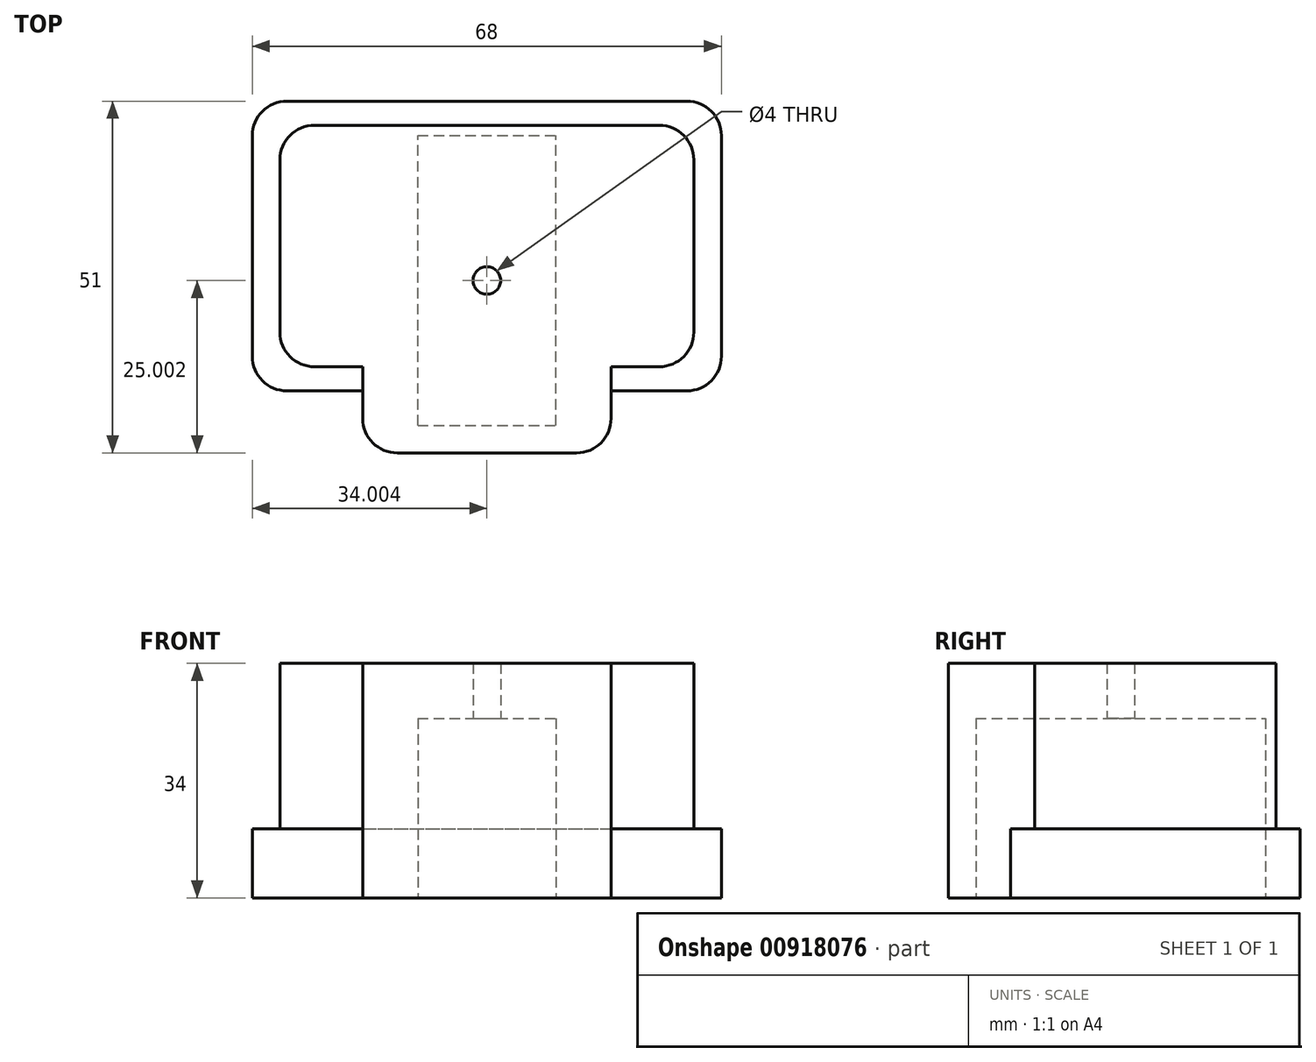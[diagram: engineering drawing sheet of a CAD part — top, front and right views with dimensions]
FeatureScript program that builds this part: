
annotation { "Feature Type Name" : "Feature", "Feature Type Description" : "" }
export const myFeature = defineFeature(function(context is Context, id is Id, definition is map)
    precondition{}
    {
        {
            var Q0;
            Q0=qCreatedBy(makeId("Top.planeOp"),FACE);
            var sketch = newSketch(context, id + "F0", { "sketchPlane" : qUnion([Q0])});
            skLineSegment(sketch, "E0.bottom", {"start": v(-57.16, -32.25) * mm, "end": v(10.84, -32.25) * mm});
            skLineSegment(sketch, "E0.top", {"start": v(-57.16, -74.25) * mm, "end": v(10.84, -74.25) * mm});
            skLineSegment(sketch, "E0.left", {"start": v(-57.16, -32.25) * mm, "end": v(-57.16, -74.25) * mm});
            skLineSegment(sketch, "E0.right", {"start": v(10.84, -32.25) * mm, "end": v(10.84, -74.25) * mm});
            skSolve(sketch);
        }
        {
            var Q0;
            Q0 = qSketchRegion(id + "F0", true);
            extrude(context, id + "F1", {"entities" : qUnion([Q0]), "flatOperationType" : FlatOperationType.REMOVE, "depth" : 10 * mm, "offsetDistance" : 25 * mm, "domain" : OperationDomain.MODEL});
        }
        {
            var Q0;
            Q0=makeQuery(id+"F1.opExtrude","CAP_FACE",FACE,{"disambiguationData":[OSD([sQuery(id+"F0.wireOp",EDGE,"E0.bottom"),sQuery(id+"F0.wireOp",EDGE,"E0.top"),sQuery(id+"F0.wireOp",EDGE,"E0.left"),sQuery(id+"F0.wireOp",EDGE,"E0.right")])],"isStart":false});
            var sketch = newSketch(context, id + "F2", { "sketchPlane" : qUnion([Q0])});
            skLineSegment(sketch, "E1", {"start": v(-57.16, -32.25) * mm, "end": v(10.84, -74.25) * mm});
            skPoint(sketch, "E2", {"position": v(-23.16, -53.25) * mm});
            skLineSegment(sketch, "E3.bottom", {"start": v(-53.16, -35.75) * mm, "end": v(6.84, -35.75) * mm});
            skLineSegment(sketch, "E3.top", {"start": v(-53.16, -70.75) * mm, "end": v(6.84, -70.75) * mm});
            skLineSegment(sketch, "E3.left", {"start": v(-53.16, -35.75) * mm, "end": v(-53.16, -70.75) * mm});
            skLineSegment(sketch, "E3.right", {"start": v(6.84, -35.75) * mm, "end": v(6.84, -70.75) * mm});
            skLineSegment(sketch, "E4", {"start": v(6.84, -35.75) * mm, "end": v(-53.16, -70.75) * mm});
            skSolve(sketch);
        }
        {
            var Q0;
            Q0 = qSketchRegion(id + "F2", true);
            extrude(context, id + "F3", {"entities" : qUnion([Q0]), "operationType" : NewBodyOperationType.ADD, "depth" : 24 * mm, "offsetDistance" : 25 * mm});
        }
        {
            var Q0;
            Q0=makeQuery(id+"F1.opExtrude","CAP_FACE",FACE,{"disambiguationData":[OSD([sQuery(id+"F0.wireOp",EDGE,"E0.bottom"),sQuery(id+"F0.wireOp",EDGE,"E0.top"),sQuery(id+"F0.wireOp",EDGE,"E0.left"),sQuery(id+"F0.wireOp",EDGE,"E0.right")])],"isStart":true});
            var sketch = newSketch(context, id + "F4", { "sketchPlane" : qUnion([Q0])});
            skLineSegment(sketch, "E5.bottom", {"start": v(-5.16, 37.25) * mm, "end": v(-41.16, 37.25) * mm});
            skLineSegment(sketch, "E5.top", {"start": v(-5.16, 83.25) * mm, "end": v(-41.16, 83.25) * mm});
            skLineSegment(sketch, "E5.left", {"start": v(-5.16, 37.25) * mm, "end": v(-5.16, 83.25) * mm});
            skLineSegment(sketch, "E5.right", {"start": v(-41.16, 37.25) * mm, "end": v(-41.16, 83.25) * mm});
            skPoint(sketch, "E6", {"position": v(-23.16, 32.25) * mm});
            skPoint(sketch, "E7", {"position": v(-23.16, 37.25) * mm});
            skSolve(sketch);
        }
        {
            var Q0;
            Q0 = qSketchRegion(id + "F4", true);
            extrude(context, id + "F5", {"entities" : qUnion([Q0]), "operationType" : NewBodyOperationType.ADD, "flatOperationType" : FlatOperationType.REMOVE, "oppositeDirection" : true, "depth" : 34 * mm, "offsetDistance" : 25 * mm, "domain" : OperationDomain.MODEL});
        }
        {
            var Q0;
            Q0=makeQuery(id+"F1.opExtrude","CAP_FACE",FACE,{"disambiguationData":[OSD([sQuery(id+"F0.wireOp",EDGE,"E0.bottom"),sQuery(id+"F0.wireOp",EDGE,"E0.top"),sQuery(id+"F0.wireOp",EDGE,"E0.left"),sQuery(id+"F0.wireOp",EDGE,"E0.right")])],"isStart":true});
            var sketch = newSketch(context, id + "F6", { "sketchPlane" : qUnion([Q0])});
            skLineSegment(sketch, "E8.bottom", {"start": v(-33.16, 79.25) * mm, "end": v(-13.16, 79.25) * mm});
            skLineSegment(sketch, "E8.top", {"start": v(-33.16, 37.25) * mm, "end": v(-13.16, 37.25) * mm});
            skLineSegment(sketch, "E8.left", {"start": v(-33.16, 79.25) * mm, "end": v(-33.16, 37.25) * mm});
            skLineSegment(sketch, "E8.right", {"start": v(-13.16, 79.25) * mm, "end": v(-13.16, 37.25) * mm});
            skSolve(sketch);
        }
        {
            var Q0;
            Q0 = qSketchRegion(id + "F6", true);
            extrude(context, id + "F7", {"entities" : qUnion([Q0]), "operationType" : NewBodyOperationType.REMOVE, "oppositeDirection" : true, "depth" : 26 * mm, "offsetDistance" : 25 * mm});
        }
        {
            var Q0;
            Q0=makeQuery(id+"F7.boolean.opBoolean","COPY",FACE,{"derivedFrom":makeQuery(id+"F7.opExtrude","CAP_FACE",FACE,{"disambiguationData":[OSD([sQuery(id+"F6.wireOp",EDGE,"E8.bottom"),sQuery(id+"F6.wireOp",EDGE,"E8.top"),sQuery(id+"F6.wireOp",EDGE,"E8.left"),sQuery(id+"F6.wireOp",EDGE,"E8.right")])],"isStart":false})});
            var sketch = newSketch(context, id + "F8", { "sketchPlane" : qUnion([Q0])});
            skLineSegment(sketch, "E9", {"start": v(-33.16, 79.25) * mm, "end": v(-13.16, 37.25) * mm});
            skCircle(sketch, "E10", {"center": v(-23.16, 58.25) * mm, "radius": 2 * mm});
            skSolve(sketch);
        }
        {
            var Q0;
            Q0 = qSketchRegion(id + "F8", true);
            extrude(context, id + "F9", {"entities" : qUnion([Q0]), "operationType" : NewBodyOperationType.REMOVE, "oppositeDirection" : true, "depth" : 25 * mm, "offsetDistance" : 25 * mm});
        }
        {
            var Q0;
            Q0=makeQuery(id+"F3.opExtrude","SWEPT_EDGE",EDGE,{"disambiguationData":[OSD([sQuery(id+"F2.wireOp",EDGE,"E3.top"),sQuery(id+"F2.wireOp",EDGE,"E3.right")])]});
            var Q1;
            Q1=makeQuery(id+"F3.opExtrude","SWEPT_EDGE",EDGE,{"disambiguationData":[OSD([sQuery(id+"F2.wireOp",EDGE,"E3.bottom"),sQuery(id+"F2.wireOp",EDGE,"E3.right"),sQuery(id+"F2.wireOp",EDGE,"E4")])]});
            var Q2;
            Q2=makeQuery(id+"F3.opExtrude","SWEPT_EDGE",EDGE,{"disambiguationData":[OSD([sQuery(id+"F2.wireOp",EDGE,"E3.bottom"),sQuery(id+"F2.wireOp",EDGE,"E3.left")])]});
            var Q3;
            Q3=makeQuery(id+"F3.opExtrude","SWEPT_EDGE",EDGE,{"disambiguationData":[OSD([sQuery(id+"F2.wireOp",EDGE,"E3.top"),sQuery(id+"F2.wireOp",EDGE,"E3.left"),sQuery(id+"F2.wireOp",EDGE,"E4")])]});
            var Q4;
            Q4=makeQuery(id+"F5.opExtrude","SWEPT_EDGE",EDGE,{"disambiguationData":[OSD([sQuery(id+"F4.wireOp",EDGE,"E5.top"),sQuery(id+"F4.wireOp",EDGE,"E5.right")])]});
            var Q5;
            Q5=makeQuery(id+"F5.opExtrude","SWEPT_EDGE",EDGE,{"disambiguationData":[OSD([sQuery(id+"F4.wireOp",EDGE,"E5.top"),sQuery(id+"F4.wireOp",EDGE,"E5.left")])]});
            var Q6;
            Q6=makeQuery(id+"F1.opExtrude","SWEPT_EDGE",EDGE,{"disambiguationData":[OSD([sQuery(id+"F0.wireOp",EDGE,"E0.top"),sQuery(id+"F0.wireOp",EDGE,"E0.left")])]});
            var Q7;
            Q7=makeQuery(id+"F1.opExtrude","SWEPT_EDGE",EDGE,{"disambiguationData":[OSD([sQuery(id+"F0.wireOp",EDGE,"E0.top"),sQuery(id+"F0.wireOp",EDGE,"E0.right")])]});
            var Q8;
            Q8=makeQuery(id+"F1.opExtrude","SWEPT_EDGE",EDGE,{"disambiguationData":[OSD([sQuery(id+"F0.wireOp",EDGE,"E0.bottom"),sQuery(id+"F0.wireOp",EDGE,"E0.right")])]});
            var Q9;
            Q9=makeQuery(id+"F1.opExtrude","SWEPT_EDGE",EDGE,{"disambiguationData":[OSD([sQuery(id+"F0.wireOp",EDGE,"E0.bottom"),sQuery(id+"F0.wireOp",EDGE,"E0.left")])]});
            fillet(context, id + "F10", {"entities" : qUnion([Q0, Q1, Q2, Q3, Q4, Q5, Q6, Q7, Q8, Q9]), "radius" : 5 * mm, "tangentPropagation" : true, "allowEdgeOverflow" : false});
        }
    });
